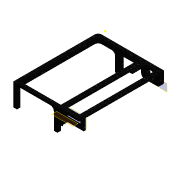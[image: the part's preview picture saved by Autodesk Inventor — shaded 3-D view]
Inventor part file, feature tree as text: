
AUTODESK INVENTOR PART (.ipt)
format: ipt  version: 2019.4 (Build 234330000, 330)  size: 416,768 bytes
history: native  units: mm
features: reference x22, other x14, sketch x11, extrude x9, projected_geometry x8, plane x3, hole x3, fillet x1, pattern_linear x1
ambient origin geometry x8: Origin, YZ Plane, XZ Plane, XY Plane, X Axis, Y Axis, Z Axis, Center Point
bodies: Solid1 (feature_tree)
feature tree (72):
  plane  "Work Plane1"
  extrude  "Extrusion1"  Depth=6.0mm
  extrude  "Extrusion2"  Depth=10.0mm TaperAngle=0.0deg
  plane  "Work Plane2"
  plane  "Work Plane5"
  extrude  "Extrusion6"  Depth=2.9mm
  extrude  "Extrusion12"  Depth=2.9mm
  hole  "Hole1"  [1 undecoded]
  extrude  "Extrusion13"  Depth=14.0mm
  fillet  "Fillet3"  Radius=53.0mm
  other  "Work Point1"
  hole  "Hole4"  [1 undecoded]
  sketch  "Sketch19"  dims[d41=3.8mm d42=6.0mm d43=7.0mm d44=4.0mm d45=90.0deg d46=50.0mm d47=20.594885mm d74=0.0mm]
  hole  "Hole5"  [1 undecoded]
  pattern_linear  "Rectangular Pattern2"  Count1=1  [1 undecoded]
  extrude  "Extrusion15"  Depth=10.0mm
  extrude  "Extrusion16"  Depth=10.0mm TaperAngle=0.0deg
  extrude  "Extrusion18"  Depth=10.0mm
  extrude  "Extrusion19"  Depth=12.0mm
  sketch  "Sketch1"  dims[d0=6.0mm d1=0.0mm d2=1.0mm]
  sketch  "Sketch2"  dims[d5=18.0mm d6=10.0mm d7=0.0mm]
  reference  "Reference4"
  reference  "Reference5"
  reference  "Reference6"
  reference  "Reference7"
  reference  "Reference8"
  reference  "Reference9"
  sketch  "Sketch6"  dims[d12=2.9mm d13=2.9mm]
  reference  "Reference33"
  reference  "Reference34"
  reference  "Reference35"
  reference  "Reference36"
  reference  "Reference37"
  reference  "Reference38"
  projected_geometry  "Projected Loop9"
  sketch  "Sketch14"  dims[d14=2.9mm d15=2.9mm]
  projected_geometry  "Projected Loop10"
  projected_geometry  "Projected Loop11"
  projected_geometry  "Projected Loop12"
  projected_geometry  "Projected Loop13"
  reference  "Reference41"
  sketch  "Sketch18"  dims[d37=10.0mm d38=0.0mm]
  projected_geometry  "Projected Loop15"
  sketch  "Sketch20"  dims[d76=14.0mm d77=14.0mm d79=53.0mm]
  reference  "Reference43"
  reference  "Reference44"
  reference  "Reference45"
  reference  "Reference46"
  reference  "Reference47"
  sketch  "Sketch21"  dims[d81=0.0mm d83=64.0mm]
  reference  "Reference48"
  reference  "Reference49"
  sketch  "Sketch22"  dims[d84=6.0mm d85=10.0mm]
  projected_geometry  "Projected Loop16"
  sketch  "Sketch24"  dims[d86=10.0mm]
  reference  "Reference52"
  sketch  "Sketch25"  dims[d87=10.0mm d88=0.0mm d90=10.0mm d91=10.0mm d92=10.0mm d93=0.0mm d94=10.0mm d95=12.0mm d96=12.0mm d97=12.0mm d110=5.0mm d111=2.8mm d112=6.0mm d113=7.0mm d114=4.0mm d115=90.0deg d116=20.0mm d117=20.594885mm d118=105.0mm d119=2.8mm d120=6.0mm d121=4.0mm d122=2.0mm d123=90.0deg d124=8.0mm d125=0.0mm d126=150.0mm d128=12.5mm d129=10.0mm d130=30.0mm d132=10.0mm d133=5.0mm d134=0.0mm d135=10.0mm d138=3.0mm d139=0.0mm d140=9.0mm d141=10.0mm d146=2.8mm d147=20.0mm d148=0.0mm d149=14.0mm d150=2.0mm d151=5.0mm d152=0.0mm d153=2.5mm d154=2.5mm d155=2.5mm d156=2.5mm]
  projected_geometry  "Projected Loop18"
  reference  "Reference53"
  other  "Assembly_opentrons_microscope_slide_y_base.iam"
  other  "00_NEMA11:1"
  other  "Lagerschild_11_1"
  other  "Assembly_spindeldrive_350mm_2:1"
  other  "00_spindel_350mm:1"
  other  "00_spindel_bearings:1"
  other  "Assembly_Opentrons_Imagingunit_v2.iam"
  other  "00_MGN12 LINEAR GUIDE RAIL, CONFIGURABLE:2"
  other  "00_spindel_bearings:2"
  other  "00_MGN12 LINEAR GUIDE RAIL, CONFIGURABLE:1"
  other  "09_Opentrons_Microscope_Baseplate:1"
  other  "00_Endstop:1"
  other  "Assembly_Opentrons_Imagingunit_v0.iam"
note: 4 required parameter values undecoded (feature->parameter linkage not recoverable at this tier; creation-order binding heuristic only, values carry confidence <= 0.55)
